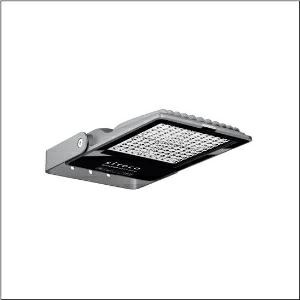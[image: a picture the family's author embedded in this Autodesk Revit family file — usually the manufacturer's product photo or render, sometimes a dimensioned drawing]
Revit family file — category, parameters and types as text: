
# Revit family: sicompact_r__31_mini___pl32_5xa7571c1k23_a489
name_source: partatom
category: Lighting Fixtures
units: mm (PartAtom-declared; Revit-internal decimal feet)

## family parameters
Cut with Voids When Loaded = No
Host = Face
Light Source = No
Part Type = Normal
Room Calculation Point = No
Round Connector Dimension = Use Diameter
Shared = No

## types (1)
- SiCompact® 31 mini  PL32 (1 x LED, 15000 lm, 100 W, 3000K)
    Apparent Load = 100 VA
    CIE Flux Codes = 32 69 98 100 100
    Color Rendering = 70
    Color Temperature = 3000K
    Default Elevation = 1800 mm
    Description = SiCompact® 31 mini, floodlight, primary light control with lens, of plastic, of toughened safety glass, transparent, light distribution: PL32, light emission: direct distribution, primary light characteristic: asymmetric, installation type: surface-mounted, LED, High Power LED, rated luminous flux: 15.000lm, luminous efficacy: 150lm/W, light colour: 730, colour temperature: 3000K, control gear: ECG, with cable, 3x 1.5mm², mains connection: 220..240V, AC, 50/60Hz, connection cable pre-assembled, cable length: 2m, rated input power: 100W, of diecast aluminium, specular, metallic grey (RAL 9006), length: 461mm, width: 261mm, height: 62mm, bracket, of sheet steel, coated, metallic grey (RAL 9006), ON/OFF, protection rating (complete): IP66, insulation class (complete): insulation class I (protective earthing), certification: CE, ENEC, impact resistance: IK08, permissible operating ambient temperature: -40..+45°C, packaging unit: 1 piece

Light Distribution: PL32
    Height = 62 mm  [stored 0.203412 ft]
    Lamp = 1 x LED
    Lamp Light Flux = 15000 lm
    Lamp Power = 100 W
    Lamp count = 1
    Length = 460 mm
    Luminous efficacy = 150 lm/W
    Manufacturer = Siteco
    ModVariant = No
    Model = 5XA7571C1K23
    Mounting Place = Wall
    Mounting Type = Surface mounted
    Number of Poles = 1
    OnlyDefault = Yes
    Power Factor = 1
    Product Name = SiCompact® 31 mini | PL32
    Product group = floodlight | wall mounted
    ProductGroupID = 2001
    Protection Class = Protection class I
    Protection Degree = IP 66
    RLX_Detail_Level = 1
    RLX_Emergency_Light_Flux = 0 lm
    RLX_Emergency_Type = 0
    RLX_Emergency_Type_DB = No
    RlxData = <blob elided: 126577 chars, md5=bfdc8d26>
    Socket = socket
    Standby Power = 0 W
    System Light Flux = 15000 lm
    System Power = 100 W
    Type Comments = Product without accessories
    Type Image = l_1006951.jpg
    URL = http://relux.com
    VarID = ---
    Voltage = 0 V
    Weight = 0.00 kg
    Width = 260 mm

note: [stored X ft] marks values corroborated as IEEE doubles in the binary element streams (Revit-internal decimal feet)

## geometry (parser evidence)
native form markers: Blend x4, Sweep x14
no freeform markers — native parametric forms only
